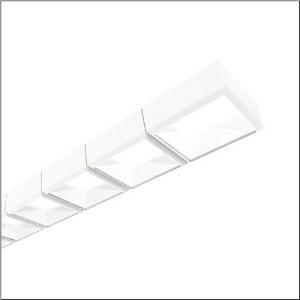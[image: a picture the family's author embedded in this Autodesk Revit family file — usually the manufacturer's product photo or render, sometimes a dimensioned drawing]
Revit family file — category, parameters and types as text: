
# Revit family: scriptus_r__11_5mz313d04wa_45ce
name_source: partatom
category: Lighting Fixtures
units: mm (PartAtom-declared; Revit-internal decimal feet)

## family parameters
Cut with Voids When Loaded = No
Host = Face
Light Source = No
Part Type = Normal
Room Calculation Point = No
Round Connector Dimension = Use Diameter
Shared = No

## types (1)
- Scriptus® 11 (1 x LED 4000K / CRI = 80 (unbekannt), 2660 lm / 4010 lm, 4000K)
    Apparent Load = 99 VA
    CIE Flux Codes = - - - 0 100 / 82 95 99 100 100
    Color Rendering = 80
    Color Temperature = 4000K
    Default Elevation = 1800 mm
    Description = Scriptus® 11, office luminaire, primary optical cover: lenses, CAT 2 (L<= 3000cd/m²), light emission: direct/indirect distribution, primary light characteristic: symmetric, installation type: suspended mounting, LED, rated luminous flux: 13.330lm, luminous efficacy: 134lm/W, light colour: 840, colour temperature: 4000K, control gear: DALI, with terminal, 5-pole, mains connection: 230V, AC, 50Hz, rated input power: 99W, LED, control gear: ECG DALI, housing, luminaire housing, of aluminium, traffic white (RAL 9016), length: 2.648mm, width: 114mm, height: 57mm, protection rating (complete): IP20, insulation class (complete): insulation class I (protective earthing), certification: CE, ENEC, VDE, protection symbol: F, permissible operating ambient temperature: 0..+35°C, standard: EN 50419, packaging unit: 1 piece
    Height = 57 mm
    Lamp = 1 x LED 4000K / CRI >= 80 (unbekannt)
    Lamp Light Flux = 2660 lm / 4010 lm
    Lamp count = 1
    Length = 2648 mm
    Luminous efficacy = 134 lm/W
    Manufacturer = Siteco
    ModVariant = No
    Model = 5MZ313D04WA
    Mounting Place = Ceiling
    Mounting Type = Pendant
    Number of Poles = 1
    OnlyDefault = Yes
    Power Factor = 1
    Product Name = Scriptus® 11
    Product group = office luminaire | ceiling pendant
    ProductGroupID = 904
    Protection Class = Protection class I
    Protection Degree = IP 20
    RLX_Detail_Level = 1
    RLX_Emergency_Light_Flux = 0 lm
    RLX_Emergency_Type = 0
    RLX_Emergency_Type_DB = No
    RlxData = <blob elided: 31593 chars, md5=40d7d8a8>
    Socket = socket
    Standby Power = 0 W
    System Light Flux = 13340 lm
    System Power = 99 W
    Type Comments = Product without accessories
    Type Image = l_1004839.jpg
    URL = http://relux.com
    VarID = ---
    Voltage = 0 V
    Weight = 0.00 kg
    Width = 114 mm

## geometry (parser evidence)
native form markers: Blend x4, Sweep x22
no freeform markers — native parametric forms only
